# Revit family: 651_5c8991e7834d46519cdca2e42b1001
name_source: partatom
category: Data Devices
revit_build: Autodesk Revit 2017 (Build: 20160225_1515(x64)
units: mm (PartAtom-declared; Revit-internal decimal feet)

## family parameters
Cut with Voids When Loaded = No
Host = Face
Maintain Annotation Orientation = Yes
Part Type = Normal
Room Calculation Point = No
Round Connector Dimension = Use Diameter
Shared = No

## types (1)
- RCC-C3DOCS
    Default Elevation = 0 mm  [stored 0 ft]
    Description = Regio Midi – Pre-programmed room controller with communication
    H1 = 30 mm  [stored 0.0984252 ft]
    H_2 = 48 mm
    L1 = 37 mm  [stored 0.121391 ft]
    L2D = 0 mm  [stored 0 ft]
    L_2 = 48 mm
    MC Active Power = 0 W
    MC CosPhi = 0.95
    MC Number of Poles = 1
    MC Product Code = RCC-C3DOCS
    MC Voltage = 230 V
    Manufacturer = Regin
    S1 = 0 mm  [stored 0 ft]
    S3 = 16 mm  [stored 0.0524934 ft]
    S4 = 5 mm  [stored 0.0164042 ft]
    SketchPlaneIDs = 10482;153b746f-b00a-47b6-946a-48530699bbd5-000028f2
    W = 38 mm  [stored 0.124672 ft]
    W1 = 12 mm  [stored 0.0393701 ft]
    W2D = 0 mm  [stored 0 ft]
    magiApparentLoad = 0 VA
    magiPartTypeId = 651
    magiProductFamilyId = 5c8991e7834d46519cdca2e42b1001
    magiProductId = 68dda085e7634900959217ba775d42

note: [stored X ft] marks values corroborated as IEEE doubles in the binary element streams (Revit-internal decimal feet)

## geometry (parser evidence)
native form markers: Sweep x2
no freeform markers — native parametric forms only
